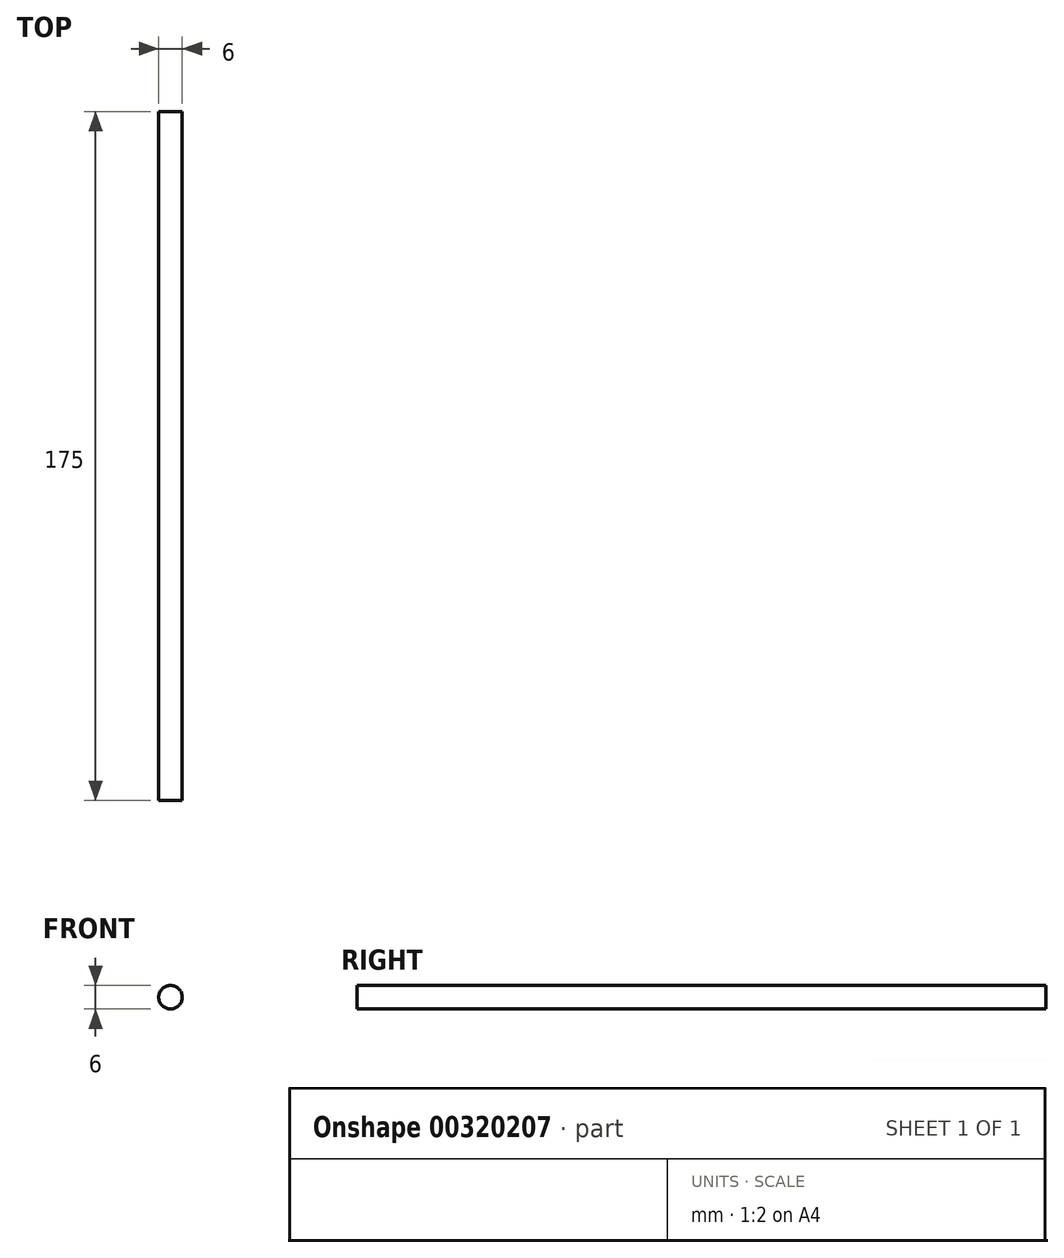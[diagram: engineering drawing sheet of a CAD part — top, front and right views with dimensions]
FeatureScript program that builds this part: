
annotation { "Feature Type Name" : "Feature", "Feature Type Description" : "" }
export const myFeature = defineFeature(function(context is Context, id is Id, definition is map)
    precondition{}
    {
        {
            var Q0;
            Q0=qCreatedBy(makeId("Front.planeOp"),FACE);
            var sketch = newSketch(context, id + "F0", { "sketchPlane" : qUnion([Q0])});
            skCircle(sketch, "E0", {"center": v(0, 0) * mm, "radius": 3 * mm});
            skSolve(sketch);
        }
        {
            var Q0;
            Q0 = qSketchRegion(id + "F0", true);
            extrude(context, id + "F1", {"entities" : qUnion([Q0]), "endBound" : BoundingType.SYMMETRIC, "depth" : 175 * mm});
        }
    });
